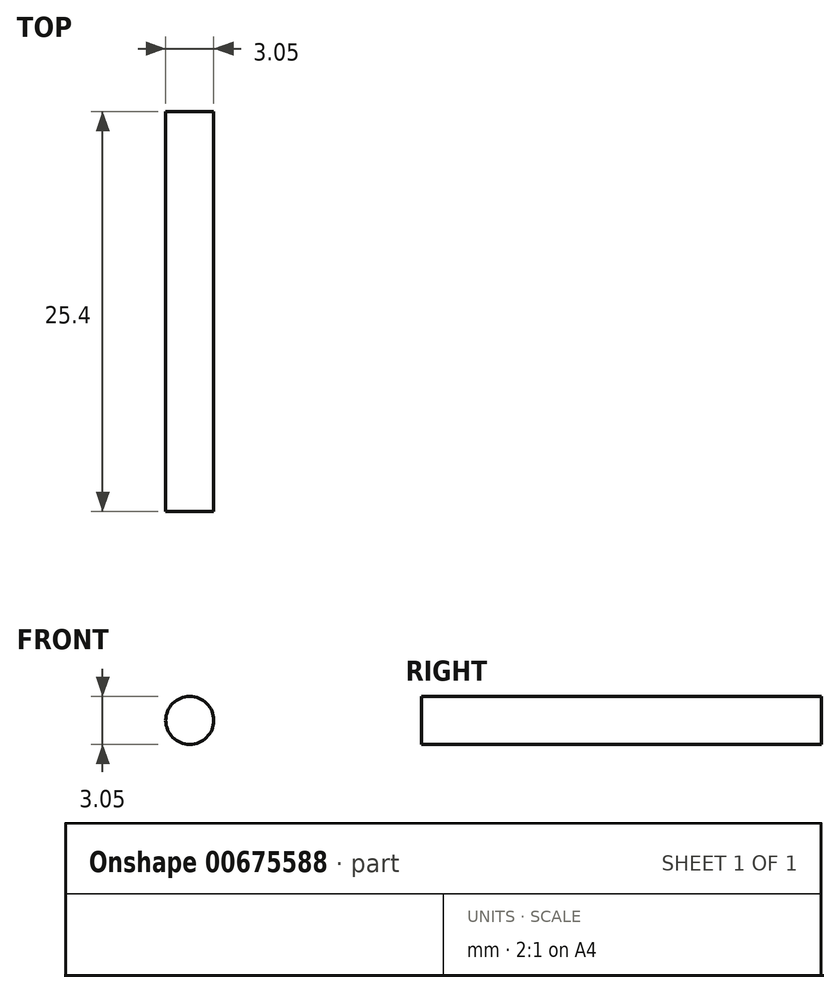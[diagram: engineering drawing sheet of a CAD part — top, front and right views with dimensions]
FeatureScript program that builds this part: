
annotation { "Feature Type Name" : "Feature", "Feature Type Description" : "" }
export const myFeature = defineFeature(function(context is Context, id is Id, definition is map)
    precondition{}
    {
        {
            var Q0;
            Q0=qCreatedBy(makeId("Front.planeOp"),FACE);
            var sketch = newSketch(context, id + "F0", { "sketchPlane" : qUnion([Q0])});
            skCircle(sketch, "E0", {"center": v(-23.4, 24.16) * mm, "radius": 1.52 * mm});
            skSolve(sketch);
        }
        {
            var Q0;
            Q0 = qSketchRegion(id + "F0", true);
            extrude(context, id + "F1", {"entities" : qUnion([Q0]), "depth" : 25.4 * mm, "offsetDistance" : 25.4 * mm});
        }
    });
